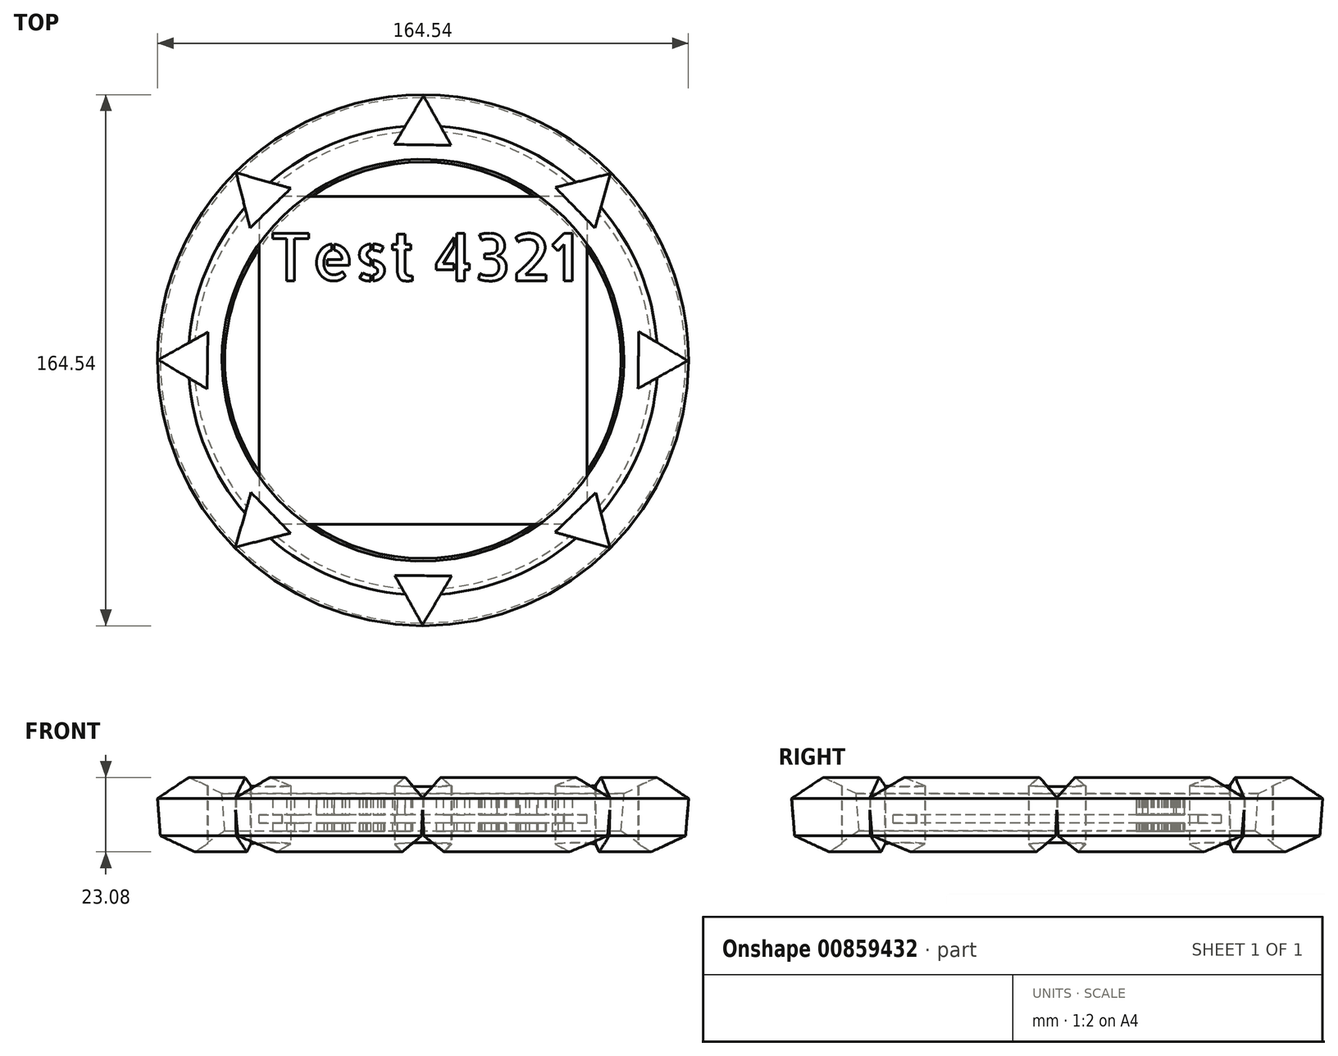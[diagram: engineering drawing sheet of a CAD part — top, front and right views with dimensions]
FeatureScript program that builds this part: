
annotation { "Feature Type Name" : "Feature", "Feature Type Description" : "" }
export const myFeature = defineFeature(function(context is Context, id is Id, definition is map)
    precondition{}
    {
        {
            var Q0;
            Q0=qCreatedBy(makeId("Top.planeOp"),FACE);
            var sketch = newSketch(context, id + "F0", { "sketchPlane" : qUnion([Q0])});
            skLineSegment(sketch, "E0.bottom", {"start": v(50.8, 50.8) * mm, "end": v(-50.8, 50.8) * mm});
            skLineSegment(sketch, "E0.top", {"start": v(50.8, -50.8) * mm, "end": v(-50.8, -50.8) * mm});
            skLineSegment(sketch, "E0.left", {"start": v(50.8, 50.8) * mm, "end": v(50.8, -50.8) * mm});
            skLineSegment(sketch, "E0.right", {"start": v(-50.8, 50.8) * mm, "end": v(-50.8, -50.8) * mm});
            skPoint(sketch, "E0.middle", {"position": v(0, 0) * mm});
            skSolve(sketch);
        }
        {
            var Q0;
            Q0=makeQuery(id+"F0.imprint","IMPRINT",FACE,{"disambiguationData":[TD([[makeQuery(id+"F0.imprint","IMPRINT",EDGE,{"derivedFrom":sQuery(id+"F0.wireOp",EDGE,"E0.bottom")}),1.0]])]});
            extrude(context, id + "F1", {"entities" : qUnion([Q0]), "depth" : 2.54 * mm, "offsetDistance" : 25.4 * mm});
        }
        {
            var Q0;
            Q0=makeQuery(id+"F1.opExtrude","CAP_FACE",FACE,{"disambiguationData":[OSD([sQuery(id+"F0.wireOp",EDGE,"E0.bottom"),sQuery(id+"F0.wireOp",EDGE,"E0.top"),sQuery(id+"F0.wireOp",EDGE,"E0.left"),sQuery(id+"F0.wireOp",EDGE,"E0.right")])],"isStart":false});
            var sketch = newSketch(context, id + "F2", { "sketchPlane" : qUnion([Q0])});
            skCircle(sketch, "E1", {"center": v(0, 0) * mm, "radius": 71.84 * mm});
            skPoint(sketch, "E2", {"position": v(-50.8, 50.8) * mm});
            skPoint(sketch, "E3", {"position": v(-71.84, 0) * mm});
            skSolve(sketch);
        }
        {
            var Q0;
            Q0=qCreatedBy(makeId("Front.planeOp"),FACE);
            var sketch = newSketch(context, id + "F3", { "sketchPlane" : qUnion([Q0])});
            skLineSegment(sketch, "E4.0", {"start": v(-61.41, -2.46) * mm, "end": v(-70.96, -9) * mm});
            skLineSegment(sketch, "E4.1", {"start": v(-70.96, -9) * mm, "end": v(-81.39, -4) * mm});
            skLineSegment(sketch, "E4.2", {"start": v(-81.39, -4) * mm, "end": v(-82.27, 7.54) * mm});
            skLineSegment(sketch, "E4.3", {"start": v(-82.27, 7.54) * mm, "end": v(-72.73, 14.08) * mm});
            skLineSegment(sketch, "E4.4", {"start": v(-72.73, 14.08) * mm, "end": v(-62.3, 9.07) * mm});
            skLineSegment(sketch, "E4.5", {"start": v(-62.3, 9.07) * mm, "end": v(-61.41, -2.46) * mm});
            skSolve(sketch);
        }
        {
            var Q0;
            Q0=makeQuery(id+"F3.imprint","IMPRINT",FACE,{"disambiguationData":[TD([[makeQuery(id+"F3.imprint","IMPRINT",EDGE,{"derivedFrom":sQuery(id+"F3.wireOp",EDGE,"E4.0")}),-1.0]])]});
            var Q1;
            Q1 = qConstructionFilter(qBodyType(qCreatedBy(id + "F3" ,EDGE), BodyType.WIRE), ConstructionObject.NO);
            var Q2;
            Q2 = qConstructionFilter(qBodyType(qCreatedBy(id + "F2" ,EDGE), BodyType.WIRE), ConstructionObject.NO);
            sweep(context, id + "F4", {"profiles" : qUnion([Q0]), "surfaceProfiles" : qUnion([Q1]), "path" : qUnion([Q2])});
        }
        {
            var Q0;
            Q0=qCreatedBy(makeId("Top.planeOp"),FACE);
            var sketch = newSketch(context, id + "F5", { "sketchPlane" : qUnion([Q0])});
            skLineSegment(sketch, "E5.0", {"start": v(-66.64, 8.73) * mm, "end": v(-66.88, -8.87) * mm});
            skLineSegment(sketch, "E5.1", {"start": v(-66.88, -8.87) * mm, "end": v(-82, 0.14) * mm});
            skLineSegment(sketch, "E5.2", {"start": v(-82, 0.14) * mm, "end": v(-66.64, 8.73) * mm});
            skLineSegment(sketch, "E6.1.0", {"start": v(-58.08, -57.89) * mm, "end": v(-53.3, -40.95) * mm});
            skLineSegment(sketch, "E6.1.1", {"start": v(-41.02, -53.56) * mm, "end": v(-58.08, -57.89) * mm});
            skLineSegment(sketch, "E6.1.2", {"start": v(-53.3, -40.95) * mm, "end": v(-41.02, -53.56) * mm});
            skLineSegment(sketch, "E6.2.0", {"start": v(-0.14, -82) * mm, "end": v(-8.73, -66.64) * mm});
            skLineSegment(sketch, "E6.2.1", {"start": v(8.87, -66.88) * mm, "end": v(-0.14, -82) * mm});
            skLineSegment(sketch, "E6.2.2", {"start": v(-8.73, -66.64) * mm, "end": v(8.87, -66.88) * mm});
            skLineSegment(sketch, "E6.3.0", {"start": v(57.89, -58.08) * mm, "end": v(40.95, -53.3) * mm});
            skLineSegment(sketch, "E6.3.1", {"start": v(53.56, -41.02) * mm, "end": v(57.89, -58.08) * mm});
            skLineSegment(sketch, "E6.3.2", {"start": v(40.95, -53.3) * mm, "end": v(53.56, -41.02) * mm});
            skLineSegment(sketch, "E6.4.0", {"start": v(82, -0.14) * mm, "end": v(66.64, -8.73) * mm});
            skLineSegment(sketch, "E6.4.1", {"start": v(66.88, 8.87) * mm, "end": v(82, -0.14) * mm});
            skLineSegment(sketch, "E6.4.2", {"start": v(66.64, -8.73) * mm, "end": v(66.88, 8.87) * mm});
            skLineSegment(sketch, "E6.5.0", {"start": v(58.08, 57.89) * mm, "end": v(53.3, 40.95) * mm});
            skLineSegment(sketch, "E6.5.1", {"start": v(41.02, 53.56) * mm, "end": v(58.08, 57.89) * mm});
            skLineSegment(sketch, "E6.5.2", {"start": v(53.3, 40.95) * mm, "end": v(41.02, 53.56) * mm});
            skLineSegment(sketch, "E6.6.0", {"start": v(0.14, 82) * mm, "end": v(8.73, 66.64) * mm});
            skLineSegment(sketch, "E6.6.1", {"start": v(-8.87, 66.88) * mm, "end": v(0.14, 82) * mm});
            skLineSegment(sketch, "E6.6.2", {"start": v(8.73, 66.64) * mm, "end": v(-8.87, 66.88) * mm});
            skLineSegment(sketch, "E6.7.0", {"start": v(-57.89, 58.08) * mm, "end": v(-40.95, 53.3) * mm});
            skLineSegment(sketch, "E6.7.1", {"start": v(-53.56, 41.02) * mm, "end": v(-57.89, 58.08) * mm});
            skLineSegment(sketch, "E6.7.2", {"start": v(-40.95, 53.3) * mm, "end": v(-53.56, 41.02) * mm});
            skPoint(sketch, "E6.center", {"position": v(0, 0) * mm});
            skSolve(sketch);
        }
        {
            var Q0;
            Q0 = qSketchRegion(id + "F5", true);
            extrude(context, id + "F6", {"entities" : qUnion([Q0]), "operationType" : NewBodyOperationType.REMOVE, "endBound" : BoundingType.SYMMETRIC, "depth" : 38.1 * mm, "offsetDistance" : 25.4 * mm});
        }
        {
            var Q0;
            Q0=makeQuery(id+"F1.opExtrude","CAP_FACE",FACE,{"disambiguationData":[OSD([sQuery(id+"F0.wireOp",EDGE,"E0.bottom"),sQuery(id+"F0.wireOp",EDGE,"E0.top"),sQuery(id+"F0.wireOp",EDGE,"E0.left"),sQuery(id+"F0.wireOp",EDGE,"E0.right")])],"isStart":false});
            var sketch = newSketch(context, id + "F7", { "sketchPlane" : qUnion([Q0])});
            skText(sketch, "E7", { "text": "Test 4321", "fontName": "AllertaStencil-Regular.ttf"});
            const initialGuessF7  = {"E7": [-0.04763, 0.02463, 1, 0, 0.0147]};
            skSetInitialGuess(sketch, initialGuessF7);
            skSolve(sketch);
        }
        {
            var Q0;
            Q0 = qSketchRegion(id + "F7", true);
            extrude(context, id + "F8", {"entities" : qUnion([Q0]), "operationType" : NewBodyOperationType.ADD, "endBound" : BoundingType.SYMMETRIC, "depth" : 10.16 * mm, "offsetDistance" : 25.4 * mm});
        }
    });
